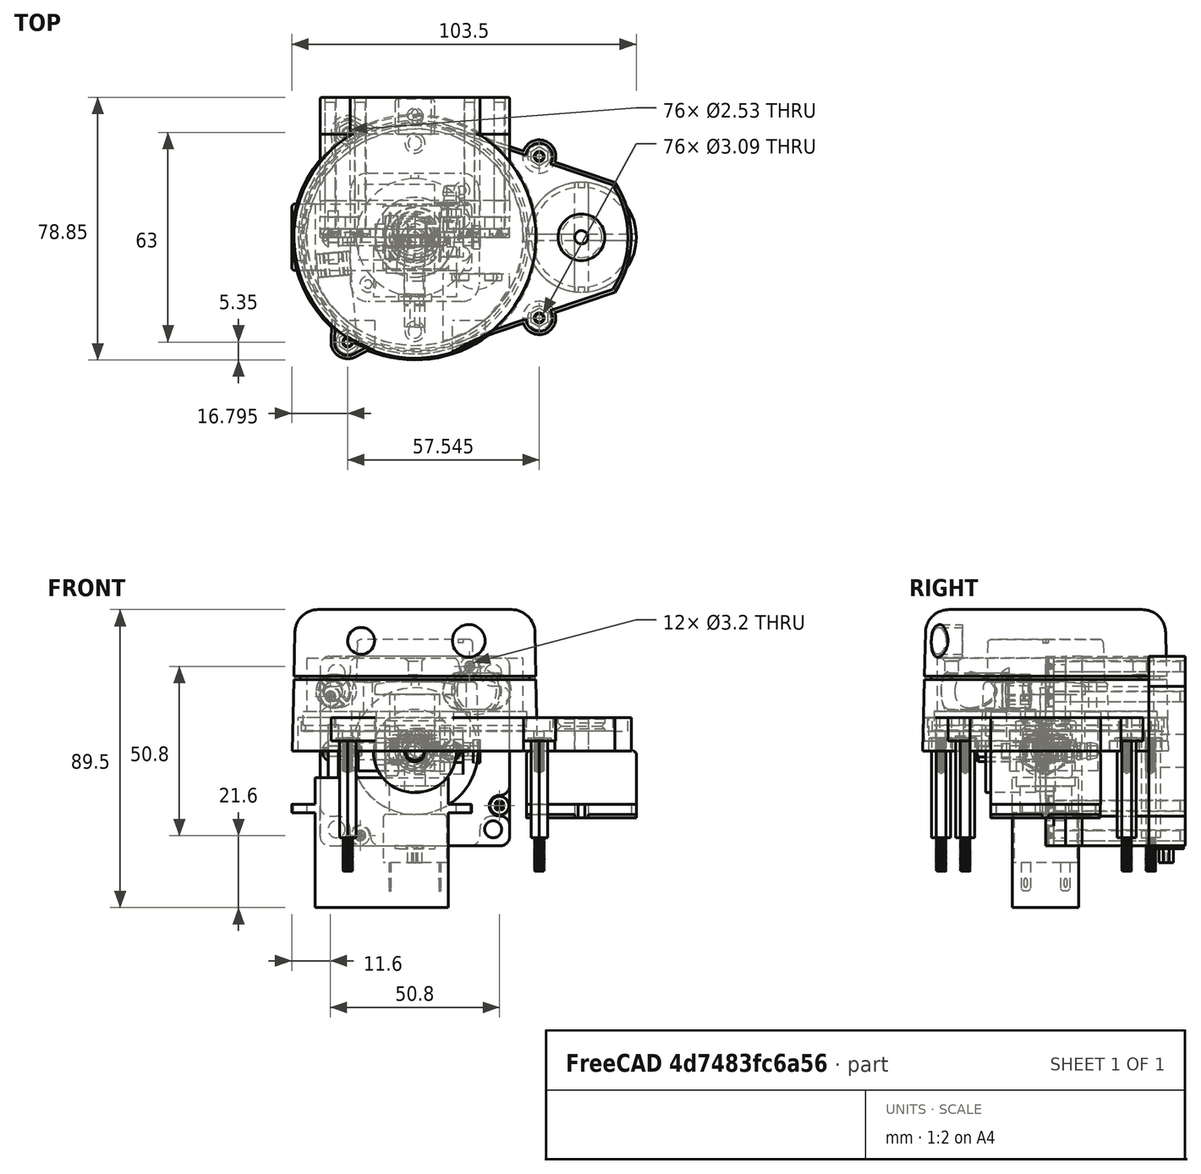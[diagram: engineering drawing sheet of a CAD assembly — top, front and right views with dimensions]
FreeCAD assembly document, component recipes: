
FREECAD ASSEMBLY — COMPONENT RECIPES ("generic-hardware")

This assembly document has 22 components, labeled P0..P21 below (a component is one placed body or linked part). 20 of them carry a construction recipe — the FreeCAD feature program that regenerates the part from scratch, quoted from this document or its linked companion documents; the rest are supplied as boundary geometry only. No exploded tour is included for this assembly.
NOTE — document 2 of 2 of this assembly tour. The two overview renders and the header above are repeated from document 1; the component sections below continue where the previous document stopped.
COMPONENT P21 — recipe-attached ("23HS16_0884S_equiped", modeled in this document).
Construction recipe (the document's own serialized feature program — sketch geometry with constraints, then the solid features built on it; lengths are millimeters unless a unit is written):

FEATURE [Sketcher::SketchObject] Sketch007
  ArcFitTolerance = 0
  AttachmentSupport = -> [XZ_Plane007]
  ExternalBSplineMaxDegree = 0
  ExternalBSplineTolerance = 0
  FullyConstrained = true
  InternalTolerance = 1e-06
  MakeInternals = false
  MapMode = 5
  Placement = pos=(0,0,0) rot=(1,0,0;1.5708rad)
  Support = -> [XZ_Plane007]
  TreeRank = 0
  sketch-geometry (5):
    g0: LineSegment StartX=28.5 StartY=28.5 StartZ=0 EndX=-28.5 EndY=28.5 EndZ=0
    g1: LineSegment StartX=-28.5 StartY=28.5 StartZ=0 EndX=-28.5 EndY=-28.5 EndZ=0
    g2: LineSegment StartX=-28.5 StartY=-28.5 StartZ=0 EndX=28.5 EndY=-28.5 EndZ=0
    g3: LineSegment StartX=28.5 StartY=-28.5 StartZ=0 EndX=28.5 EndY=28.5 EndZ=0
    g4: Circle [constr] CenterX=2.6926e-12 CenterY=-1.717e-13 CenterZ=0 NormalX=0 NormalY=0 NormalZ=1 AngleXU=0 Radius=40.3051
  constraints (14):
    c: Coincident(g0,g1)
    c: Coincident(g1,g2)
    c: Coincident(g2,g3)
    c: Coincident(g3,g0)
    c: Equal(g0,g1)
    c: Equal(g0,g2)
    c: Equal(g0,g3)
    c: PointOnObject(g0,g4)
    c: PointOnObject(g1,g4)
    c: PointOnObject(g2,g4)
    c: PointOnObject(g3,g4)
    c: Coincident(g4,g-1)
    c: Horizontal(g0)
    c: DistanceX(g0,g0) = 57
FEATURE [PartDesign::Pad] Pad005
  AddSubType = 0
  AutoTaperInnerAngle = false
  CheckUpToFaceLimits = true
  ClaimChildren = false
  Direction = (1,1,1)
  Fit = 0
  FitJoin = 0
  InnerFit = 0
  InnerFitJoin = 0
  Length = 11
  Length2 = 100
  NewSolid = false
  Placement = pos=(0,0,0) rot=(1,0,0;1.5708rad)
  Profile = -> Sketch007
  Refine = true
  Reversed = true
  Suppress = false
  TaperInnerAngle = 0
  TaperInnerAngleRev = 0
  TreeRank = 0
  Type = 0
  UsePipeForDraft = true
  _ProfileBasedVersion = 0
FEATURE [Sketcher::SketchObject] Sketch008
  ArcFitTolerance = 0
  AttachmentSupport = -> [Pad005]
  ExternalBSplineMaxDegree = 0
  ExternalBSplineTolerance = 0
  ExternalGeometry = -> [Pad005]
  FullyConstrained = true
  InternalTolerance = 1e-06
  MakeInternals = false
  MapMode = 5
  Placement = pos=(0,11,2.4e-15) rot=(-1,0,0;1.5708rad)
  Support = -> [Pad005]
  TreeRank = 0
  sketch-geometry (5):
    g0: LineSegment StartX=-28.5 StartY=28.5 StartZ=0 EndX=-28.5 EndY=19.5 EndZ=0
    g1: LineSegment StartX=-28.5 StartY=19.5 StartZ=0 EndX=-23.5 EndY=19.5 EndZ=0
    g2: LineSegment StartX=-28.5 StartY=28.5 StartZ=0 EndX=-19.5 EndY=28.5 EndZ=0
    g3: LineSegment StartX=-19.5 StartY=28.5 StartZ=0 EndX=-19.5 EndY=23.5 EndZ=0
    g4: ArcOfCircle CenterX=-23.5 CenterY=23.5 CenterZ=0 NormalX=0 NormalY=0 NormalZ=1 AngleXU=0 Radius=4 StartAngle=4.71239 EndAngle=6.28319
  constraints (13):
    c: Vertical(g0)
    c: Coincident(g1,g0)
    c: Horizontal(g1)
    c: Coincident(g2,g0)
    c: Coincident(g3,g2)
    c: Vertical(g3)
    c: Horizontal(g2)
    c: Coincident(g0,g-4)
    c: Equal(g2,g0)
    c: Tangent(g4,g3) = 1.5708
    c: Tangent(g4,g1) = -1.5708
    c: DistanceY(g0,g0) = 9
    c: DistanceX(g4) = -23.5
FEATURE [PartDesign::Pocket] Pocket002
  AddSubType = 1
  AutoTaperInnerAngle = false
  BaseFeature = -> Pad005
  CheckUpToFaceLimits = true
  ClaimChildren = false
  Fit = 0
  FitJoin = 0
  InnerFit = 0
  InnerFitJoin = 0
  Length = 5
  Length2 = 100
  NewSolid = false
  Placement = pos=(0,0,0) rot=(1,0,0;1.5708rad)
  Profile = -> Sketch008
  Refine = true
  Suppress = false
  TaperInnerAngle = 0
  TaperInnerAngleRev = 0
  TreeRank = 0
  Type = 0
  _ProfileBasedVersion = 0
  _Version = 0
FEATURE [PartDesign::PolarPattern] PolarPattern007
  AddSubType = 0
  Angle = 360
  Axis = -> Sketch008 [N_Axis]
  BaseFeature = -> Pocket002
  CopyShape = false
  NewSolid = false
  Occurrences = 4
  OriginalSubs = -> [Pocket002]
  Originals = -> [Pocket002]
  ParallelTransform = true
  Placement = pos=(0,0,0) rot=(1,0,0;1.5708rad)
  Refine = true
  SubTransform = true
  Suppress = false
  TreeRank = 0
  _Version = 0
FEATURE [Sketcher::SketchObject] Sketch009
  ArcFitTolerance = 0
  AttachmentSupport = -> [XZ_Plane007]
  ExternalBSplineMaxDegree = 0
  ExternalBSplineTolerance = 0
  FullyConstrained = true
  InternalTolerance = 1e-06
  MakeInternals = false
  MapMode = 5
  Placement = pos=(0,0,0) rot=(1,0,0;1.5708rad)
  Support = -> [XZ_Plane007]
  TreeRank = 0
  sketch-geometry (2):
    g0: Circle CenterX=23.5 CenterY=23.5 CenterZ=0 NormalX=0 NormalY=0 NormalZ=1 AngleXU=0 Radius=2.55
    g1: LineSegment [constr] StartX=-1.146e-13 StartY=5.53e-14 StartZ=0 EndX=23.5 EndY=23.5 EndZ=0
  constraints (5):
    c: DistanceX(g0) = 23.5
    c: Coincident(g1,g-1)
    c: Coincident(g1,g0)
    c: Angle(g-1,g1) = 0.785398
    c: Diameter(g0) = 5.1
FEATURE [PartDesign::Pocket] Pocket003
  AddSubType = 1
  AutoTaperInnerAngle = false
  BaseFeature = -> PolarPattern007
  CheckUpToFaceLimits = true
  ClaimChildren = false
  Fit = 0
  FitJoin = 0
  InnerFit = 0
  InnerFitJoin = 0
  Length = 5
  Length2 = 100
  NewSolid = false
  Placement = pos=(0,0,0) rot=(1,0,0;1.5708rad)
  Profile = -> Sketch009
  Refine = true
  Suppress = false
  TaperInnerAngle = 0
  TaperInnerAngleRev = 0
  TreeRank = 0
  Type = 1
  _ProfileBasedVersion = 0
  _Version = 0
FEATURE [PartDesign::PolarPattern] PolarPattern008
  AddSubType = 0
  Angle = 360
  Axis = -> Sketch009 [N_Axis]
  BaseFeature = -> Pocket003
  CopyShape = false
  NewSolid = false
  Occurrences = 4
  OriginalSubs = -> [Pocket003]
  Originals = -> [Pocket003]
  ParallelTransform = true
  Placement = pos=(0,0,0) rot=(1,0,0;1.5708rad)
  Refine = true
  SubTransform = true
  Suppress = false
  TreeRank = 0
  _Version = 0
FEATURE [Sketcher::SketchObject] Sketch010
  ArcFitTolerance = 0
  AttachmentSupport = -> [XZ_Plane007]
  ExternalBSplineMaxDegree = 0
  ExternalBSplineTolerance = 0
  FullyConstrained = true
  InternalTolerance = 1e-06
  MakeInternals = false
  MapMode = 5
  Placement = pos=(0,0,0) rot=(1,0,0;1.5708rad)
  Support = -> [XZ_Plane007]
  TreeRank = 0
  sketch-geometry (1):
    g0: Circle CenterX=0 CenterY=0 CenterZ=0 NormalX=0 NormalY=0 NormalZ=1 AngleXU=0 Radius=19
  constraints (2):
    c: Coincident(g0,g-1)
    c: Diameter(g0) = 38
FEATURE [PartDesign::Pad] Pad006
  AddSubType = 0
  AutoTaperInnerAngle = false
  BaseFeature = -> PolarPattern008
  CheckUpToFaceLimits = true
  ClaimChildren = false
  Direction = (1,1,1)
  Fit = 0
  FitJoin = 0
  InnerFit = 0
  InnerFitJoin = 0
  Length = 1.6
  Length2 = 100
  NewSolid = false
  Placement = pos=(0,0,0) rot=(1,0,0;1.5708rad)
  Profile = -> Sketch010
  Refine = true
  Suppress = false
  TaperInnerAngle = 0
  TaperInnerAngleRev = 0
  TreeRank = 0
  Type = 0
  UsePipeForDraft = true
  _ProfileBasedVersion = 0
FEATURE [Sketcher::SketchObject] Sketch011
  ArcFitTolerance = 0
  AttachmentSupport = -> [XZ_Plane007]
  ExternalBSplineMaxDegree = 0
  ExternalBSplineTolerance = 0
  FullyConstrained = true
  InternalTolerance = 1e-06
  MakeInternals = false
  MapMode = 5
  Placement = pos=(0,0,0) rot=(1,0,0;1.5708rad)
  Support = -> [XZ_Plane007]
  TreeRank = 0
  sketch-geometry (1):
    g0: Circle CenterX=0 CenterY=0 CenterZ=0 NormalX=0 NormalY=0 NormalZ=1 AngleXU=0 Radius=5
  constraints (2):
    c: Coincident(g0,g-1)
    c: Diameter(g0) = 10
FEATURE [PartDesign::Pocket] Pocket004
  AddSubType = 1
  AutoTaperInnerAngle = false
  BaseFeature = -> Pad006
  CheckUpToFaceLimits = true
  ClaimChildren = false
  Fit = 0
  FitJoin = 0
  InnerFit = 0
  InnerFitJoin = 0
  Length = 5
  Length2 = 100
  NewSolid = false
  Placement = pos=(0,0,0) rot=(1,0,0;1.5708rad)
  Profile = -> Sketch011
  Refine = true
  Reversed = true
  Suppress = false
  TaperInnerAngle = 0
  TaperInnerAngleRev = 0
  TreeRank = 0
  Type = 1
  _ProfileBasedVersion = 0
  _Version = 0
FEATURE [PartDesign::Fillet] Fillet
  AddSubType = 0
  Base = -> Pocket004 [Edge2,Edge8,Edge51,Edge17]
  BaseFeature = -> Pocket004
  NewSolid = false
  Placement = pos=(0,0,0) rot=(1,0,0;1.5708rad)
  Radius = 3
  Refine = true
  SupportTransform = false
  Suppress = false
  TreeRank = 0
FEATURE [Sketcher::SketchObject] Sketch012
  ArcFitTolerance = 0
  AttachmentSupport = -> [XZ_Plane007]
  ExternalBSplineMaxDegree = 0
  ExternalBSplineTolerance = 0
  ExternalGeometry = -> [Fillet]
  FullyConstrained = true
  InternalTolerance = 1e-06
  MakeInternals = false
  MapMode = 5
  Placement = pos=(0,0,0) rot=(1,0,0;1.5708rad)
  Support = -> [XZ_Plane007]
  TreeRank = 0
  sketch-geometry (5):
    g0: ArcOfCircle CenterX=16.4 CenterY=28.5 CenterZ=0 NormalX=0 NormalY=0 NormalZ=1 AngleXU=0 Radius=3.1 StartAngle=0 EndAngle=3.14159
    g1: ArcOfCircle CenterX=16.4 CenterY=25.4 CenterZ=0 NormalX=0 NormalY=0 NormalZ=1 AngleXU=0 Radius=3.1 StartAngle=3.14159 EndAngle=6.28319
    g2: LineSegment StartX=13.3 StartY=28.5 StartZ=0 EndX=13.3 EndY=25.4 EndZ=0
    g3: LineSegment StartX=19.5 StartY=28.5 StartZ=0 EndX=19.5 EndY=25.4 EndZ=0
    g4: Circle [constr] CenterX=16.4 CenterY=25.4 CenterZ=0 NormalX=0 NormalY=0 NormalZ=1 AngleXU=0 Radius=3.1
  constraints (12):
    c: Tangent(g0,g3) = 1.5708
    c: Tangent(g0,g2) = -1.5708
    c: Tangent(g2,g1) = -1.5708
    c: Tangent(g3,g1) = 1.5708
    c: Vertical(g2)
    c: Equal(g0,g1)
    c: PointOnObject(g0,g-3)
    c: Coincident(g4,g1)
    c: PointOnObject(g1,g4)
    c: PointOnObject(g0,g4)
    c: Diameter(g1) = 6.2
    c: DistanceX(g-1,g1) = 16.4
FEATURE [PartDesign::Pocket] Pocket005
  AddSubType = 1
  AutoTaperInnerAngle = false
  BaseFeature = -> Fillet
  CheckUpToFaceLimits = true
  ClaimChildren = false
  Fit = 0
  FitJoin = 0
  InnerFit = 0
  InnerFitJoin = 0
  Length = 2.5
  Length2 = 100
  NewSolid = false
  Placement = pos=(0,0,0) rot=(1,0,0;1.5708rad)
  Profile = -> Sketch012
  Refine = true
  Suppress = false
  TaperInnerAngle = 0
  TaperInnerAngleRev = 0
  TreeRank = 0
  Type = 0
  _ProfileBasedVersion = 0
  _Version = 0
FEATURE [PartDesign::PolarPattern] PolarPattern009
  AddSubType = 0
  Angle = 360
  Axis = -> Sketch012 [N_Axis]
  BaseFeature = -> Pocket005
  CopyShape = false
  NewSolid = false
  Occurrences = 4
  OriginalSubs = -> [Pocket005]
  Originals = -> [Pocket005]
  ParallelTransform = true
  Placement = pos=(0,0,0) rot=(1,0,0;1.5708rad)
  Refine = true
  SubTransform = true
  Suppress = false
  TreeRank = 0
  _Version = 0
FEATURE [Sketcher::SketchObject] Sketch013
  ArcFitTolerance = 0
  AttachmentSupport = -> [XZ_Plane007]
  ExternalBSplineMaxDegree = 0
  ExternalBSplineTolerance = 0
  ExternalGeometry = -> [PolarPattern009]
  FullyConstrained = true
  InternalTolerance = 1e-06
  MakeInternals = false
  MapMode = 5
  Placement = pos=(0,0,0) rot=(1,0,0;1.5708rad)
  Support = -> [XZ_Plane007]
  TreeRank = 0
  sketch-geometry (1):
    g0: Circle CenterX=16.4 CenterY=25.4 CenterZ=0 NormalX=0 NormalY=0 NormalZ=1 AngleXU=0 Radius=1.6
  constraints (2):
    c: Coincident(g0,g-3)
    c: Diameter(g0) = 3.2
FEATURE [PartDesign::Pocket] Pocket006
  AddSubType = 1
  AutoTaperInnerAngle = false
  BaseFeature = -> PolarPattern009
  CheckUpToFaceLimits = true
  ClaimChildren = false
  Fit = 0
  FitJoin = 0
  InnerFit = 0
  InnerFitJoin = 0
  Length = 5
  Length2 = 100
  NewSolid = false
  Placement = pos=(0,0,0) rot=(1,0,0;1.5708rad)
  Profile = -> Sketch013
  Refine = true
  Suppress = false
  TaperInnerAngle = 0
  TaperInnerAngleRev = 0
  TreeRank = 0
  Type = 1
  _ProfileBasedVersion = 0
  _Version = 0
FEATURE [PartDesign::PolarPattern] PolarPattern010
  AddSubType = 0
  Angle = 360
  Axis = -> Sketch013 [N_Axis]
  BaseFeature = -> Pocket006
  CopyShape = false
  NewSolid = false
  Occurrences = 4
  OriginalSubs = -> [Pocket006]
  Originals = -> [Pocket006]
  ParallelTransform = true
  Placement = pos=(0,0,0) rot=(1,0,0;1.5708rad)
  Refine = true
  SubTransform = true
  Suppress = false
  TreeRank = 0
  _Version = 0
FEATURE [PartDesign::Fillet] Fillet001
  AddSubType = 0
  Base = -> PolarPattern010 [Edge10,Edge113,Edge8,Edge87,Edge114,Edge100,Edge86,Edge101,Edge97,Edge95,Edge81,Edge83,Edge2,Edge4,Edge110,Edge112]
  BaseFeature = -> PolarPattern010
  NewSolid = false
  Placement = pos=(0,0,0) rot=(1,0,0;1.5708rad)
  Radius = 3
  Refine = true
  SupportTransform = false
  Suppress = false
  TreeRank = 0
FEATURE [PartDesign::Body] Core  label="FrontPanel"
  AutoGroupSolids = false
  ClaimAllChildren = false
  ExportMode = 0
  Group = -> [Sketch007,Pad005,Sketch008,Pocket002,PolarPattern007,Sketch009,Pocket003,PolarPattern008,Sketch010,Pad006,Sketch011,Pocket004,Fillet,Sketch012,Pocket005,PolarPattern009,Sketch013,Pocket006,PolarPattern010,Fillet001]
  Origin = -> Origin010
  SingleSolid = true
  Tip = -> Fillet001
  TreeRank = 0
  _ExportChildren = -> [Pad005,Pocket002,PolarPattern007,Pocket003,PolarPattern008,Pad006,Pocket004,Fillet,Pocket005,PolarPattern009,Pocket006,PolarPattern010,Fillet001]
  _GroupVersion = 1
FEATURE [PartDesign::ShapeBinder] ShapeBinder
  Placement = pos=(0,0,0) rot=(1,0,0;1.5708rad)
  Support = -> [Fillet001]
  TraceSupport = false
  TreeRank = 0
FEATURE [PartDesign::Pad] Pad007
  AddSubType = 0
  AutoTaperInnerAngle = false
  CheckUpToFaceLimits = true
  ClaimChildren = false
  Direction = (1,1,1)
  Fit = 0
  FitJoin = 0
  InnerFit = 0
  InnerFitJoin = 0
  Length = 20
  Length2 = 100
  NewSolid = false
  Placement = pos=(0,0,0) rot=(1,0,0;1.5708rad)
  Profile = -> ShapeBinder
  Refine = true
  Suppress = false
  TaperInnerAngle = 0
  TaperInnerAngleRev = 0
  TreeRank = 0
  Type = 0
  UsePipeForDraft = true
  _ProfileBasedVersion = 0
FEATURE [PartDesign::Body] Body006  label="MiddleCore"
  AutoGroupSolids = false
  ClaimAllChildren = false
  ExportMode = 0
  Group = -> [ShapeBinder,Pad007]
  Origin = -> Origin011
  SingleSolid = true
  Tip = -> Pad007
  TreeRank = 0
  _ExportChildren = -> [Pad007]
  _GroupVersion = 1
FEATURE [PartDesign::ShapeBinder] ShapeBinder001
  Placement = pos=(0,20,4.4e-15) rot=(1,0,0;1.5708rad)
  Support = -> [Pad007]
  TraceSupport = false
  TreeRank = 0
FEATURE [PartDesign::Pad] Pad008
  AddSubType = 0
  AutoTaperInnerAngle = false
  CheckUpToFaceLimits = true
  ClaimChildren = false
  Direction = (1,1,1)
  Fit = 0
  FitJoin = 0
  InnerFit = 0
  InnerFitJoin = 0
  Length = 11
  Length2 = 100
  NewSolid = false
  Placement = pos=(0,20,4.4e-15) rot=(1,0,0;1.5708rad)
  Profile = -> ShapeBinder001
  Refine = true
  Suppress = false
  TaperInnerAngle = 0
  TaperInnerAngleRev = 0
  TreeRank = 0
  Type = 0
  UsePipeForDraft = true
  _ProfileBasedVersion = 0
FEATURE [Sketcher::SketchObject] Sketch014
  ArcFitTolerance = 0
  AttachmentSupport = -> [XZ_Plane009]
  ExternalBSplineMaxDegree = 0
  ExternalBSplineTolerance = 0
  FullyConstrained = true
  InternalTolerance = 1e-06
  MakeInternals = false
  MapMode = 5
  Placement = pos=(0,0,0) rot=(1,0,0;1.5708rad)
  Support = -> [XZ_Plane009]
  TreeRank = 0
  sketch-geometry (1):
    g0: Circle CenterX=0 CenterY=0 CenterZ=0 NormalX=0 NormalY=0 NormalZ=1 AngleXU=0 Radius=5
  constraints (2):
    c: Coincident(g0,g-1)
    c: Diameter(g0) = 10
FEATURE [PartDesign::Pocket] Pocket007
  AddSubType = 1
  AutoTaperInnerAngle = false
  BaseFeature = -> Pad008
  CheckUpToFaceLimits = true
  ClaimChildren = false
  Fit = 0
  FitJoin = 0
  InnerFit = 0
  InnerFitJoin = 0
  Length = 5
  Length2 = 100
  NewSolid = false
  Placement = pos=(0,20,4.4e-15) rot=(1,0,0;1.5708rad)
  Profile = -> Sketch014
  Refine = true
  Suppress = false
  TaperInnerAngle = 0
  TaperInnerAngleRev = 0
  TreeRank = 0
  Type = 1
  _ProfileBasedVersion = 0
  _Version = 0
FEATURE [PartDesign::Fillet] Fillet002
  AddSubType = 0
  Base = -> Pocket007 [Edge51,Edge61]
  BaseFeature = -> Pocket007
  NewSolid = false
  Placement = pos=(0,20,4.4e-15) rot=(1,0,0;1.5708rad)
  Radius = 0.5
  Refine = true
  SupportTransform = false
  Suppress = false
  TreeRank = 0
FEATURE [PartDesign::Body] Body007  label="RearPanel"
  AutoGroupSolids = false
  ClaimAllChildren = false
  ExportMode = 0
  Group = -> [ShapeBinder001,Pad008,Sketch014,Pocket007,Fillet002]
  Origin = -> Origin012
  SingleSolid = true
  Tip = -> Fillet002
  TreeRank = 0
  _ExportChildren = -> [Pad008,Pocket007,Fillet002]
  _GroupVersion = 1
FEATURE [Sketcher::SketchObject] Sketch015
  ArcFitTolerance = 0
  AttachmentSupport = -> [XZ_Plane010]
  ExternalBSplineMaxDegree = 0
  ExternalBSplineTolerance = 0
  FullyConstrained = true
  InternalTolerance = 1e-06
  MakeInternals = false
  MapMode = 5
  Placement = pos=(0,0,0) rot=(1,0,0;1.5708rad)
  Support = -> [XZ_Plane010]
  TreeRank = 0
  sketch-geometry (1):
    g0: Circle CenterX=0 CenterY=0 CenterZ=0 NormalX=0 NormalY=0 NormalZ=1 AngleXU=0 Radius=3.175
  constraints (2):
    c: Coincident(g0,g-1)
    c: Diameter(g0) = 6.35
FEATURE [PartDesign::Pad] Pad009
  AddSubType = 0
  AutoTaperInnerAngle = false
  CheckUpToFaceLimits = true
  ClaimChildren = false
  Direction = (1,1,1)
  Fit = 0
  FitJoin = 0
  InnerFit = 0
  InnerFitJoin = 0
  Length = 20.6
  Length2 = 100
  NewSolid = false
  Placement = pos=(0,0,0) rot=(1,0,0;1.5708rad)
  Profile = -> Sketch015
  Refine = true
  Suppress = false
  TaperInnerAngle = 0
  TaperInnerAngleRev = 0
  TreeRank = 0
  Type = 0
  UsePipeForDraft = true
  _ProfileBasedVersion = 0
FEATURE [Sketcher::SketchObject] Sketch016
  ArcFitTolerance = 0
  AttachmentSupport = -> [XY_Plane010]
  ExternalBSplineMaxDegree = 0
  ExternalBSplineTolerance = 0
  ExternalGeometry = -> [Pad009]
  FullyConstrained = true
  InternalTolerance = 1e-06
  MakeInternals = false
  MapMode = 5
  Support = -> [XY_Plane010]
  TreeRank = 0
  sketch-geometry (4):
    g0: LineSegment StartX=3.175 StartY=-20.6 StartZ=0 EndX=2.675 EndY=-20.6 EndZ=0
    g1: LineSegment StartX=2.675 StartY=-20.6 StartZ=0 EndX=2.675 EndY=-5.6 EndZ=0
    g2: LineSegment StartX=2.675 StartY=-5.6 StartZ=0 EndX=3.175 EndY=-5.6 EndZ=0
    g3: LineSegment StartX=3.175 StartY=-5.6 StartZ=0 EndX=3.175 EndY=-20.6 EndZ=0
  constraints (11):
    c: Coincident(g0,g1)
    c: Coincident(g1,g2)
    c: Coincident(g2,g3)
    c: Coincident(g3,g0)
    c: Horizontal(g0)
    c: Horizontal(g2)
    c: Vertical(g1)
    c: Vertical(g3)
    c: Coincident(g0,g-3)
    c: DistanceX(g-3,g0) = 5.85
    c: DistanceY(g3,g3) = 15
FEATURE [PartDesign::Pocket] Pocket008
  AddSubType = 1
  AutoTaperInnerAngle = false
  BaseFeature = -> Pad009
  CheckUpToFaceLimits = true
  ClaimChildren = false
  Fit = 0
  FitJoin = 0
  InnerFit = 0
  InnerFitJoin = 0
  Length = 5
  Length2 = 100
  Midplane = true
  NewSolid = false
  Placement = pos=(0,0,0) rot=(1,0,0;1.5708rad)
  Profile = -> Sketch016
  Refine = true
  Suppress = false
  TaperInnerAngle = 0
  TaperInnerAngleRev = 0
  TreeRank = 0
  Type = 1
  _ProfileBasedVersion = 0
  _Version = 0
FEATURE [PartDesign::Chamfer] Chamfer
  AddSubType = 0
  Angle = 45
  Base = -> Pocket008 [Edge5]
  BaseFeature = -> Pocket008
  ChamferType = 0
  FlipDirection = false
  NewSolid = false
  Placement = pos=(0,0,0) rot=(1,0,0;1.5708rad)
  Refine = true
  Size = 0.4
  Size2 = 1
  SupportTransform = false
  Suppress = false
  TreeRank = 0
FEATURE [PartDesign::Body] Body008  label="Axle"
  AutoGroupSolids = false
  ClaimAllChildren = false
  ExportMode = 0
  Group = -> [Sketch015,Pad009,Sketch016,Pocket008,Chamfer]
  Origin = -> Origin013
  SingleSolid = true
  Tip = -> Chamfer
  TreeRank = 0
  _ExportChildren = -> [Pad009,Pocket008,Chamfer]
  _GroupVersion = 1
FEATURE [PartDesign::ShapeBinder] ShapeBinder002
  Placement = pos=(0,20,4.4e-15) rot=(1,0,0;1.5708rad)
  Support = -> [Fillet002]
  TraceSupport = false
  TreeRank = 0
FEATURE [Sketcher::SketchObject] Sketch017
  ArcFitTolerance = 0
  AttachmentSupport = -> [ShapeBinder002]
  ExternalBSplineMaxDegree = 0
  ExternalBSplineTolerance = 0
  ExternalGeometry = -> [ShapeBinder002]
  FullyConstrained = true
  InternalTolerance = 1e-06
  MakeInternals = false
  MapMode = 5
  Placement = pos=(-2.7551e-12,20,-28.5) rot=(1,0,0;3.14159rad)
  Support = -> [ShapeBinder002]
  TreeRank = 0
  sketch-geometry (5):
    g0: LineSegment StartX=-6 StartY=-11 StartZ=0 EndX=6 EndY=-11 EndZ=0
    g1: LineSegment StartX=6 StartY=-11 StartZ=0 EndX=6 EndY=-21.5 EndZ=0
    g2: LineSegment StartX=6 StartY=-21.5 StartZ=0 EndX=-6 EndY=-21.5 EndZ=0
    g3: LineSegment StartX=-6 StartY=-21.5 StartZ=0 EndX=-6 EndY=-11 EndZ=0
    g4: Circle CenterX=4.8501e-12 CenterY=-16.25 CenterZ=0 NormalX=0 NormalY=0 NormalZ=1 AngleXU=0 Radius=2.5
  constraints (13):
    c: Coincident(g0,g1)
    c: Coincident(g1,g2)
    c: Coincident(g2,g3)
    c: Coincident(g3,g0)
    c: Horizontal(g2)
    c: Vertical(g1)
    c: Vertical(g3)
    c: Symmetric(g0,g0,g-2)
    c: PointOnObject(g2,g-4)
    c: PointOnObject(g0,g-3)
    c: DistanceX(g2,g2) = 12
    c: Symmetric(g2,g0,g4)
    c: Diameter(g4) = 5
FEATURE [PartDesign::Pad] Pad010
  AddSubType = 0
  AutoTaperInnerAngle = false
  CheckUpToFaceLimits = true
  ClaimChildren = false
  Direction = (1,1,1)
  Fit = 0
  FitJoin = 0
  InnerFit = 0
  InnerFitJoin = 0
  Length = 0.8
  Length2 = 100
  NewSolid = false
  Placement = pos=(0,20,4.4e-15) rot=(1,0,0;1.5708rad)
  Profile = -> Sketch017
  Refine = true
  Suppress = false
  TaperInnerAngle = 0
  TaperInnerAngleRev = 0
  TreeRank = 0
  Type = 0
  UsePipeForDraft = true
  _ProfileBasedVersion = 0
FEATURE [PartDesign::Fillet] Fillet003
  AddSubType = 0
  Base = -> Pad010 [Edge5,Edge2,Edge8,Edge1]
  BaseFeature = -> Pad010
  NewSolid = false
  Placement = pos=(0,20,4.4e-15) rot=(1,0,0;1.5708rad)
  Radius = 1
  Refine = true
  SupportTransform = false
  Suppress = false
  TreeRank = 0
FEATURE [PartDesign::Body] Body009  label="ProtectCable"
  AutoGroupSolids = false
  ClaimAllChildren = false
  ExportMode = 0
  Group = -> [ShapeBinder002,Sketch017,Pad010,Fillet003]
  Origin = -> Origin014
  SingleSolid = true
  Tip = -> Fillet003
  TreeRank = 0
  _ExportChildren = -> [ShapeBinder002,Pad010,Fillet003]
  _GroupVersion = 1
FEATURE [PartDesign::ShapeBinder] ShapeBinder003
  Support = -> [Fillet003]
  TraceSupport = false
  TreeRank = 0
FEATURE [Sketcher::SketchObject] Sketch018
  ArcFitTolerance = 0
  AttachmentSupport = -> [ShapeBinder003]
  ExternalBSplineMaxDegree = 0
  ExternalBSplineTolerance = 0
  ExternalGeometry = -> [ShapeBinder003]
  FullyConstrained = true
  InternalTolerance = 1e-06
  MakeInternals = false
  MapMode = 5
  Placement = pos=(-2.7591e-12,9.4e-15,-28.5) rot=(0,0,1;0rad)
  Support = -> [ShapeBinder003]
  TreeRank = 0
  sketch-geometry (5):
    g0: Circle [constr] CenterX=4.9993e-12 CenterY=36.25 CenterZ=0 NormalX=0 NormalY=0 NormalZ=1 AngleXU=0 Radius=0.35
    g1: Circle CenterX=-6.77e-14 CenterY=37.5 CenterZ=0 NormalX=0 NormalY=0 NormalZ=1 AngleXU=0 Radius=0.9
    g2: Circle [constr] CenterX=1.25 CenterY=36.25 CenterZ=0 NormalX=0 NormalY=0 NormalZ=1 AngleXU=0 Radius=0.9
    g3: Circle [constr] CenterX=-1.25 CenterY=36.25 CenterZ=0 NormalX=0 NormalY=0 NormalZ=1 AngleXU=0 Radius=0.9
    g4: Circle [constr] CenterX=8.325e-13 CenterY=35 CenterZ=0 NormalX=0 NormalY=0 NormalZ=1 AngleXU=0 Radius=0.9
  constraints (13):
    c: Coincident(g0,g-3)
    c: PointOnObject(g1,g-2)
    c: Tangent(g1,g0)
    c: Tangent(g2,g0)
    c: Tangent(g3,g0)
    c: PointOnObject(g4,g-2)
    c: Tangent(g4,g0)
    c: Equal(g4,g2)
    c: Equal(g3,g1)
    c: Symmetric(g2,g3,g-3)
    c: Horizontal(g3,g2)
    c: Diameter(g1) = 1.8
    c: DistanceY(g-3,g1) = 1.25
FEATURE [PartDesign::Line] DatumLine
  AttacherType = Attacher::AttachEngineLine
  AttachmentSupport = -> [ShapeBinder003]
  Length = 10
  MapMode = 19
  MinimumLength = 10
  Placement = pos=(2.0948e-12,36.25,-28.5) rot=(-1,0,0;3.14159rad)
  ResizeMode = 0
  Support = -> [ShapeBinder003]
  TreeRank = 0
FEATURE [PartDesign::Pad] Pad011
  AddSubType = 0
  AutoTaperInnerAngle = false
  CheckUpToFaceLimits = true
  ClaimChildren = false
  Direction = (1,1,1)
  Fit = 0
  FitJoin = 0
  InnerFit = 0
  InnerFitJoin = 0
  Length = 5
  Length2 = 100
  NewSolid = false
  Profile = -> Sketch018
  Refine = true
  Reversed = true
  Suppress = false
  TaperInnerAngle = 0
  TaperInnerAngleRev = 0
  TreeRank = 0
  Type = 0
  UsePipeForDraft = true
  _ProfileBasedVersion = 0
FEATURE [PartDesign::PolarPattern] PolarPattern011
  AddSubType = 0
  Angle = 360
  Axis = -> DatumLine
  BaseFeature = -> Pad011
  CopyShape = false
  NewSolid = false
  Occurrences = 4
  OriginalSubs = -> [Pad011]
  Originals = -> [Pad011]
  ParallelTransform = true
  Refine = true
  SubTransform = true
  Suppress = false
  TreeRank = 0
  _Version = 0
FEATURE [PartDesign::Body] Body010  label="Cables"
  AutoGroupSolids = false
  ClaimAllChildren = false
  ExportMode = 0
  Group = -> [ShapeBinder003,Sketch018,DatumLine,Pad011,PolarPattern011]
  Origin = -> Origin006
  SingleSolid = true
  Tip = -> PolarPattern011
  TreeRank = 0
  _ExportChildren = -> [ShapeBinder003,DatumLine,Pad011,PolarPattern011]
  _GroupVersion = 1
FEATURE [Sketcher::SketchObject] Sketch020
  ArcFitTolerance = 0
  AttachmentSupport = -> [XY_Plane013]
  ExternalBSplineMaxDegree = 0
  ExternalBSplineTolerance = 0
  FullyConstrained = true
  InternalTolerance = 1e-06
  MakeInternals = false
  MapMode = 5
  Support = -> [XY_Plane013]
  TreeRank = 0
  sketch-geometry (4):
    g0: LineSegment StartX=3 StartY=0 StartZ=0 EndX=12.5 EndY=0 EndZ=0
    g1: LineSegment StartX=12.5 StartY=0 StartZ=0 EndX=12.5 EndY=-15 EndZ=0
    g2: LineSegment StartX=12.5 StartY=-15 StartZ=0 EndX=3 EndY=-15 EndZ=0
    g3: LineSegment StartX=3 StartY=-15 StartZ=0 EndX=3 EndY=0 EndZ=0
  constraints (12):
    c: PointOnObject(g0,g-1)
    c: PointOnObject(g0,g-1)
    c: Vertical(g1)
    c: Coincident(g1,g2)
    c: Horizontal(g2)
    c: Coincident(g2,g3)
    c: Coincident(g3,g0)
    c: Vertical(g3)
    c: DistanceX(g0) = 3
    c: DistanceY(g2) = -15
    c: DistanceX(g1) = 12.5
    c: Coincident(g0,g1)
FEATURE [PartDesign::Revolution] Revolution
  AddSubType = 0
  Angle = 360
  Axis = (0,1,0)
  Base = (0,0,0)
  ClaimChildren = false
  Fit = 0
  FitJoin = 0
  InnerFit = 0
  InnerFitJoin = 0
  NewSolid = false
  Profile = -> Sketch020
  ReferenceAxis = -> Sketch020 [V_Axis]
  Refine = true
  Reversed = true
  Suppress = false
  TreeRank = 0
  _ProfileBasedVersion = 0
FEATURE [PartDesign::Body] Body011  label="Poulie_T5_14T_10mm"
  AutoGroupSolids = false
  ClaimAllChildren = false
  ExportMode = 0
  Group = -> [Sketch020,Revolution]
  Origin = -> Origin017
  Placement = pos=(0,-3,0) rot=(0,0,1;0rad)
  SingleSolid = true
  Tip = -> Revolution
  TreeRank = 0
  _ExportChildren = -> [Revolution]
  _GroupVersion = 1
PROVENANCE & LICENSES
A FreeCAD (.FCStd) document from a public repository crawl; recipes are the document's own serialized feature recipes (and, for linked parts, companion documents' recipes).
License: mit.
